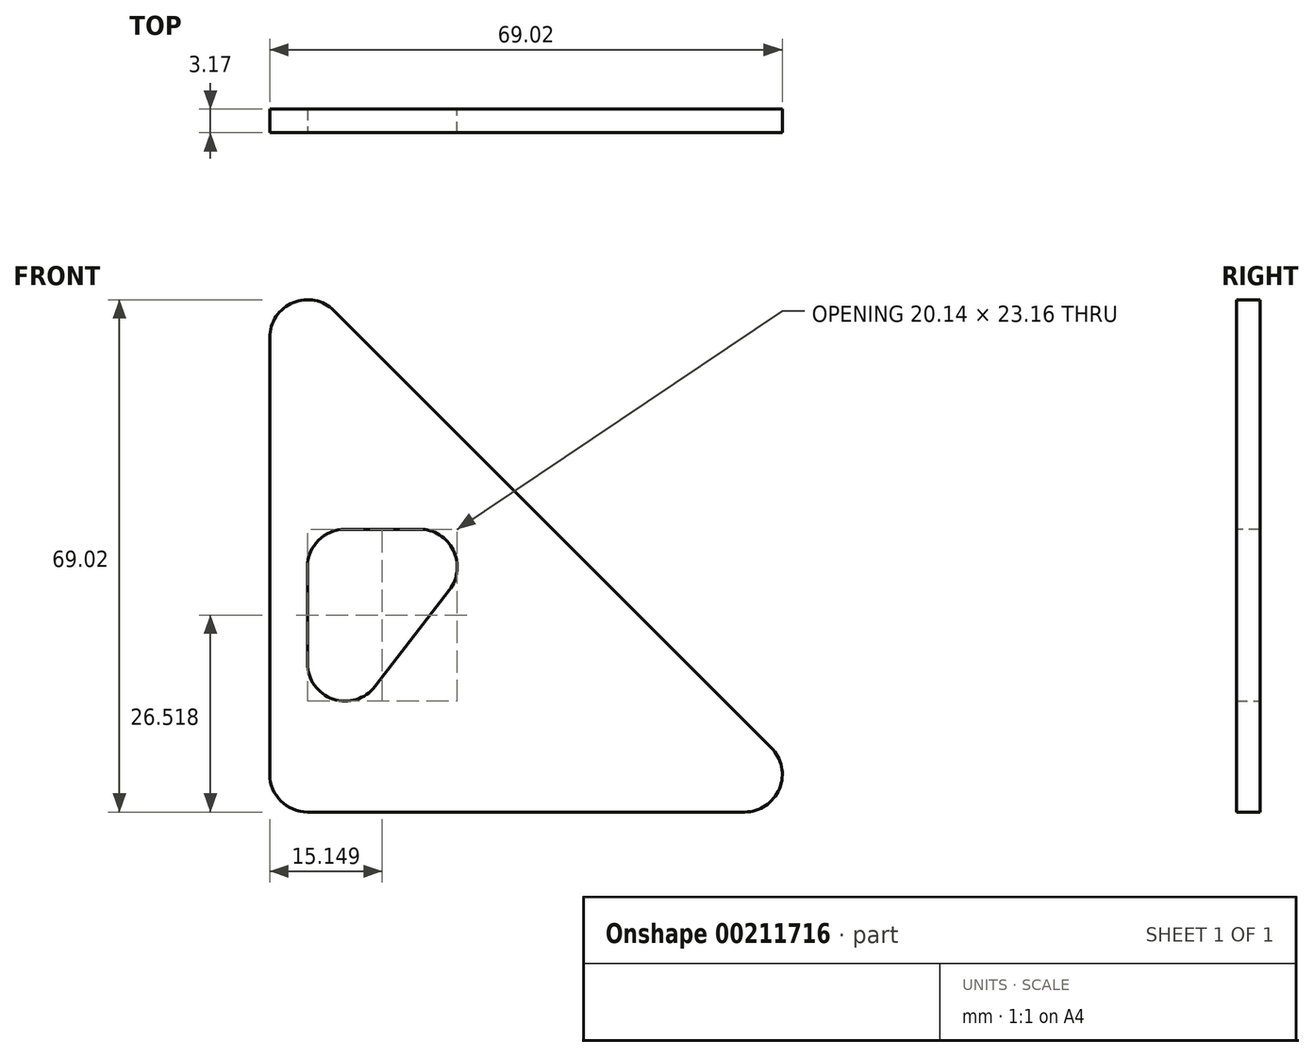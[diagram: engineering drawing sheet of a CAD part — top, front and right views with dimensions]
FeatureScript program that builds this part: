
annotation { "Feature Type Name" : "Feature", "Feature Type Description" : "" }
export const myFeature = defineFeature(function(context is Context, id is Id, definition is map)
    precondition{}
    {
        {
            var Q0;
            Q0=qCreatedBy(makeId("Front.planeOp"),FACE);
            var sketch = newSketch(context, id + "F0", { "sketchPlane" : qUnion([Q0])});
            skLineSegment(sketch, "E0", {"start": v(0, 0) * mm, "end": v(-76.2, 0) * mm});
            skLineSegment(sketch, "E1", {"start": v(-76.2, 0) * mm, "end": v(-76.2, 76.2) * mm});
            skLineSegment(sketch, "E2", {"start": v(-76.2, 76.2) * mm, "end": v(0, 0) * mm});
            skSolve(sketch);
        }
        {
            var Q0;
            Q0=makeQuery(id+"F0.imprint","IMPRINT",FACE,{"disambiguationData":[TD([[makeQuery(id+"F0.imprint","IMPRINT",EDGE,{"derivedFrom":sQuery(id+"F0.wireOp",EDGE,"E0")}),-1.0]])]});
            extrude(context, id + "F1", {"entities" : qUnion([Q0]), "depth" : 3.17 * mm});
        }
        {
            var Q0;
            Q0=makeQuery(id+"F1.opExtrude","SWEPT_EDGE",EDGE,{"disambiguationData":[OSD([sQuery(id+"F0.wireOp",EDGE,"E1"),sQuery(id+"F0.wireOp",EDGE,"E2")])]});
            var Q1;
            Q1=makeQuery(id+"F1.opExtrude","SWEPT_EDGE",EDGE,{"disambiguationData":[OSD([sQuery(id+"F0.wireOp",EDGE,"E0"),sQuery(id+"F0.wireOp",EDGE,"E1")])]});
            var Q2;
            Q2=makeQuery(id+"F1.opExtrude","SWEPT_EDGE",EDGE,{"disambiguationData":[OSD([sQuery(id+"F0.wireOp",EDGE,"E0"),sQuery(id+"F0.wireOp",EDGE,"E2")])]});
            fillet(context, id + "F2", {"entities" : qUnion([Q0, Q1, Q2]), "radius" : 5.08 * mm, "tangentPropagation" : true, "allowEdgeOverflow" : false});
        }
        {
            var Q0;
            Q0=makeQuery(id+"F1.opExtrude","CAP_FACE",FACE,{"disambiguationData":[OSD([sQuery(id+"F0.wireOp",EDGE,"E0"),sQuery(id+"F0.wireOp",EDGE,"E1"),sQuery(id+"F0.wireOp",EDGE,"E2")])],"isStart":false});
            var sketch = newSketch(context, id + "F3", { "sketchPlane" : qUnion([Q0])});
            skLineSegment(sketch, "E3", {"start": v(-76.2, 5.08) * mm, "end": v(-71.12, 5.08) * mm, "construction": true});
            skLineSegment(sketch, "E4", {"start": v(-71.12, 5.08) * mm, "end": v(-71.12, 0) * mm, "construction": true});
            skLineSegment(sketch, "E5", {"start": v(-71.12, 5.08) * mm, "end": v(-71.12, 38.1) * mm});
            skPoint(sketch, "E5.endSnap0", {"position": v(-38.1, 38.1) * mm});
            skLineSegment(sketch, "E6", {"start": v(-71.12, 38.1) * mm, "end": v(-45.72, 38.1) * mm});
            skLineSegment(sketch, "E7", {"start": v(-45.72, 38.1) * mm, "end": v(-71.12, 5.08) * mm});
            skSolve(sketch);
        }
        {
            var Q0;
            Q0=makeQuery(id+"F3.imprint","IMPRINT",FACE,{"disambiguationData":[TD([[makeQuery(id+"F3.imprint","IMPRINT",EDGE,{"derivedFrom":sQuery(id+"F3.wireOp",EDGE,"E5")}),-1.0]])]});
            extrude(context, id + "F4", {"entities" : qUnion([Q0]), "operationType" : NewBodyOperationType.REMOVE, "oppositeDirection" : true, "depth" : 25.4 * mm});
        }
        {
            var Q0;
            Q0=makeQuery(id+"F4.boolean.opBoolean","COPY",EDGE,{"derivedFrom":makeQuery(id+"F4.opExtrude","SWEPT_EDGE",EDGE,{"disambiguationData":[OSD([sQuery(id+"F3.wireOp",EDGE,"E5"),sQuery(id+"F3.wireOp",EDGE,"E7")])]})});
            var Q1;
            Q1=makeQuery(id+"F4.boolean.opBoolean","COPY",EDGE,{"derivedFrom":makeQuery(id+"F4.opExtrude","SWEPT_EDGE",EDGE,{"disambiguationData":[OSD([sQuery(id+"F3.wireOp",EDGE,"E6"),sQuery(id+"F3.wireOp",EDGE,"E7")])]})});
            var Q2;
            Q2=makeQuery(id+"F4.boolean.opBoolean","COPY",EDGE,{"derivedFrom":makeQuery(id+"F4.opExtrude","SWEPT_EDGE",EDGE,{"disambiguationData":[OSD([sQuery(id+"F3.wireOp",EDGE,"E5"),sQuery(id+"F3.wireOp",EDGE,"E6")])]})});
            fillet(context, id + "F5", {"entities" : qUnion([Q0, Q1, Q2]), "radius" : 5.08 * mm, "tangentPropagation" : true, "allowEdgeOverflow" : false});
        }
    });
